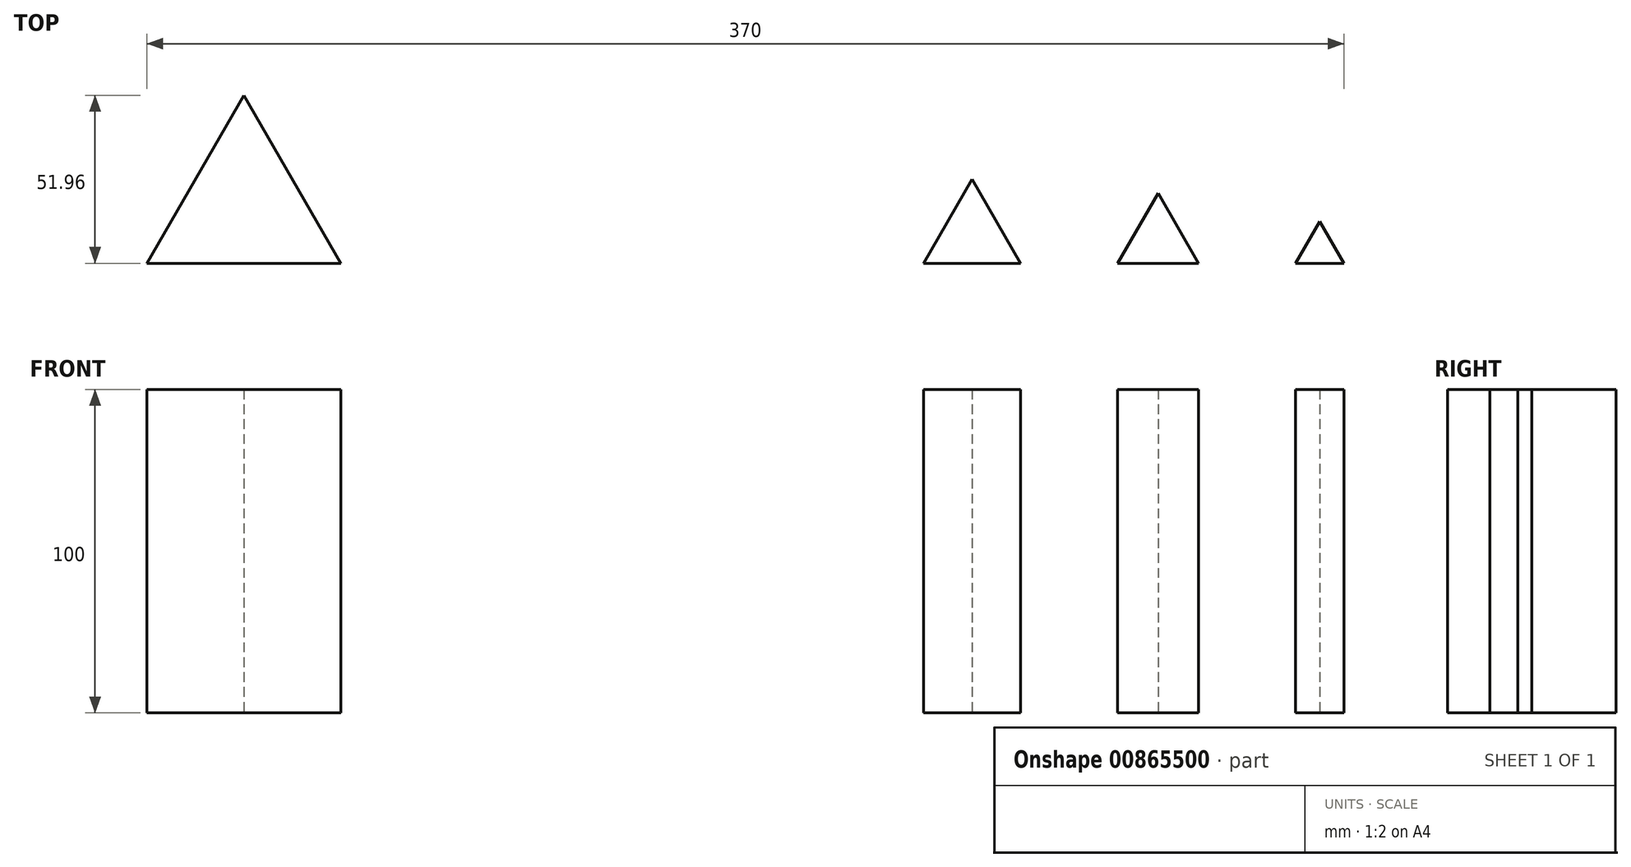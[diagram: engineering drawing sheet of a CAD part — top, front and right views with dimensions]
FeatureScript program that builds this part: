
annotation { "Feature Type Name" : "Feature", "Feature Type Description" : "" }
export const myFeature = defineFeature(function(context is Context, id is Id, definition is map)
    precondition{}
    {
        {
            var Q0;
            Q0=qCreatedBy(makeId("Top.planeOp"),FACE);
            var sketch = newSketch(context, id + "F0", { "sketchPlane" : qUnion([Q0])});
            skLineSegment(sketch, "E0.bottom", {"start": v(0, 0) * mm, "end": v(450, 0) * mm});
            skLineSegment(sketch, "E0.top", {"start": v(0, -450) * mm, "end": v(450, -450) * mm});
            skLineSegment(sketch, "E0.left", {"start": v(0, 0) * mm, "end": v(0, -450) * mm});
            skLineSegment(sketch, "E0.right", {"start": v(450, 0) * mm, "end": v(450, -450) * mm});
            skCircle(sketch, "E1", {"center": v(32.5, 0) * mm, "radius": 7.5 * mm});
            skCircle(sketch, "E2", {"center": v(70, 0) * mm, "radius": 10 * mm});
            skCircle(sketch, "E3", {"center": v(112.5, 0) * mm, "radius": 12.5 * mm});
            skCircle(sketch, "E4", {"center": v(212.5, 0) * mm, "radius": 17.5 * mm});
            skCircle(sketch, "E5", {"center": v(270, 0) * mm, "radius": 20 * mm});
            skPoint(sketch, "E6", {"position": v(0, -225) * mm});
            skCircle(sketch, "E7", {"center": v(160, 0) * mm, "radius": 15 * mm});
            skCircle(sketch, "E8", {"center": v(332.5, 0) * mm, "radius": 22.5 * mm});
            skCircle(sketch, "E9", {"center": v(400, 0) * mm, "radius": 25 * mm});
            skCircle(sketch, "E10", {"center": v(0, -50) * mm, "radius": 27.5 * mm});
            skCircle(sketch, "E11", {"center": v(0, -127.5) * mm, "radius": 30 * mm});
            skCircle(sketch, "E12", {"center": v(0, -210) * mm, "radius": 32.5 * mm});
            skCircle(sketch, "E13", {"center": v(0, -297.5) * mm, "radius": 35 * mm});
            skCircle(sketch, "E14", {"center": v(0, -390) * mm, "radius": 37.5 * mm});
            skCircle(sketch, "E15.cCircle", {"center": v(450, -45) * mm, "radius": 20 * mm, "construction": true});
            skLineSegment(sketch, "E15.0", {"start": v(450, -65) * mm, "end": v(432.68, -55) * mm});
            skLineSegment(sketch, "E15.1", {"start": v(432.68, -55) * mm, "end": v(432.68, -35) * mm});
            skLineSegment(sketch, "E15.2", {"start": v(432.68, -35) * mm, "end": v(450, -25) * mm});
            skLineSegment(sketch, "E15.3", {"start": v(450, -25) * mm, "end": v(467.32, -35) * mm});
            skLineSegment(sketch, "E15.4", {"start": v(467.32, -35) * mm, "end": v(467.32, -55) * mm});
            skLineSegment(sketch, "E15.5", {"start": v(467.32, -55) * mm, "end": v(450, -65) * mm});
            skCircle(sketch, "E16.cCircle", {"center": v(450, -120) * mm, "radius": 34.64 * mm, "construction": true});
            skLineSegment(sketch, "E16.0", {"start": v(420.17, -137.61) * mm, "end": v(419.83, -102.97) * mm});
            skLineSegment(sketch, "E16.1", {"start": v(419.83, -102.97) * mm, "end": v(449.66, -85.36) * mm});
            skLineSegment(sketch, "E16.2", {"start": v(449.66, -85.36) * mm, "end": v(479.83, -102.39) * mm});
            skLineSegment(sketch, "E16.3", {"start": v(479.83, -102.39) * mm, "end": v(480.17, -137.03) * mm});
            skLineSegment(sketch, "E16.4", {"start": v(480.17, -137.03) * mm, "end": v(450.34, -154.64) * mm});
            skLineSegment(sketch, "E16.5", {"start": v(450.34, -154.64) * mm, "end": v(420.17, -137.61) * mm});
            skCircle(sketch, "E17.cCircle", {"center": v(450, -225) * mm, "radius": 46.19 * mm, "construction": true});
            skLineSegment(sketch, "E17.0", {"start": v(410.35, -248.7) * mm, "end": v(409.66, -202.51) * mm});
            skLineSegment(sketch, "E17.1", {"start": v(409.66, -202.51) * mm, "end": v(449.3, -178.82) * mm});
            skLineSegment(sketch, "E17.2", {"start": v(449.3, -178.82) * mm, "end": v(489.65, -201.3) * mm});
            skLineSegment(sketch, "E17.3", {"start": v(489.65, -201.3) * mm, "end": v(490.34, -247.49) * mm});
            skLineSegment(sketch, "E17.4", {"start": v(490.34, -247.49) * mm, "end": v(450.7, -271.18) * mm});
            skLineSegment(sketch, "E17.5", {"start": v(450.7, -271.18) * mm, "end": v(410.35, -248.7) * mm});
            skCircle(sketch, "E18.cCircle", {"center": v(450, -360) * mm, "radius": 57.74 * mm, "construction": true});
            skLineSegment(sketch, "E18.0", {"start": v(400.24, -330.72) * mm, "end": v(450.48, -302.27) * mm});
            skLineSegment(sketch, "E18.1", {"start": v(450.48, -302.27) * mm, "end": v(500.24, -331.55) * mm});
            skLineSegment(sketch, "E18.2", {"start": v(500.24, -331.55) * mm, "end": v(499.76, -389.28) * mm});
            skLineSegment(sketch, "E18.3", {"start": v(499.76, -389.28) * mm, "end": v(449.52, -417.73) * mm});
            skLineSegment(sketch, "E18.4", {"start": v(449.52, -417.73) * mm, "end": v(399.76, -388.45) * mm});
            skLineSegment(sketch, "E18.5", {"start": v(399.76, -388.45) * mm, "end": v(400.24, -330.72) * mm});
            skLineSegment(sketch, "E19", {"start": v(420, -450) * mm, "end": v(412.5, -437) * mm});
            skLineSegment(sketch, "E20", {"start": v(412.5, -437) * mm, "end": v(405, -450) * mm});
            skLineSegment(sketch, "E21", {"start": v(420, -450) * mm, "end": v(405, -450) * mm});
            skLineSegment(sketch, "E22", {"start": v(375, -450) * mm, "end": v(362.5, -428.35) * mm});
            skLineSegment(sketch, "E23", {"start": v(362.5, -428.35) * mm, "end": v(350, -450) * mm});
            skLineSegment(sketch, "E24", {"start": v(350, -450) * mm, "end": v(375, -450) * mm});
            skLineSegment(sketch, "E25", {"start": v(320, -450) * mm, "end": v(305, -424.02) * mm});
            skLineSegment(sketch, "E26", {"start": v(305, -424.02) * mm, "end": v(290, -450) * mm});
            skLineSegment(sketch, "E27", {"start": v(290, -450) * mm, "end": v(320, -450) * mm});
            skLineSegment(sketch, "E28", {"start": v(260, -450) * mm, "end": v(220, -450) * mm});
            skLineSegment(sketch, "E29", {"start": v(220, -450) * mm, "end": v(240, -415.36) * mm});
            skLineSegment(sketch, "E30", {"start": v(240, -415.36) * mm, "end": v(260, -450) * mm});
            skLineSegment(sketch, "E31", {"start": v(190, -450) * mm, "end": v(140, -450) * mm});
            skLineSegment(sketch, "E32", {"start": v(140, -450) * mm, "end": v(165, -406.7) * mm});
            skLineSegment(sketch, "E33", {"start": v(165, -406.7) * mm, "end": v(190, -450) * mm});
            skLineSegment(sketch, "E34", {"start": v(110, -450) * mm, "end": v(50, -450) * mm});
            skLineSegment(sketch, "E35", {"start": v(50, -450) * mm, "end": v(80, -398.04) * mm});
            skLineSegment(sketch, "E36", {"start": v(80, -398.04) * mm, "end": v(110, -450) * mm});
            skCircle(sketch, "E37", {"center": v(366.86, -63.19) * mm, "radius": 8.5 * mm});
            skCircle(sketch, "E38", {"center": v(306.86, -63.19) * mm, "radius": 11.5 * mm});
            skCircle(sketch, "E39", {"center": v(237.86, -63.19) * mm, "radius": 17.5 * mm});
            skCircle(sketch, "E40", {"center": v(172.86, -63.19) * mm, "radius": 22.5 * mm});
            skCircle(sketch, "E41", {"center": v(90.36, -63.19) * mm, "radius": 30 * mm});
            skPoint(sketch, "E42.cornerSnap0", {"position": v(400, -359.59) * mm});
            skEllipse(sketch, "E43", {"center": v(355, -158.3) * mm, "majorRadius": 69.57 * mm, "minorRadius": 24.91 * mm, "majorAxis": v(0, -1)});
            skEllipse(sketch, "E44", {"center": v(255, -158.3) * mm, "majorRadius": 57.98 * mm, "minorRadius": 25.3 * mm, "majorAxis": v(0, -1)});
            skEllipse(sketch, "E45", {"center": v(160, -158.3) * mm, "majorRadius": 47.06 * mm, "minorRadius": 19.98 * mm, "majorAxis": v(0, -1)});
            skEllipse(sketch, "E46", {"center": v(75, -158.3) * mm, "majorRadius": 42.97 * mm, "minorRadius": 16.37 * mm, "majorAxis": v(0, -1)});
            skLineSegment(sketch, "E47.bottom", {"start": v(132.9, -316.06) * mm, "end": v(52.9, -316.06) * mm});
            skLineSegment(sketch, "E47.top", {"start": v(132.9, -236.06) * mm, "end": v(52.9, -236.06) * mm});
            skLineSegment(sketch, "E47.left", {"start": v(132.9, -316.06) * mm, "end": v(132.9, -236.06) * mm});
            skLineSegment(sketch, "E47.right", {"start": v(52.9, -316.06) * mm, "end": v(52.9, -236.06) * mm});
            skPoint(sketch, "E47.middle", {"position": v(92.9, -276.06) * mm});
            skLineSegment(sketch, "E48.bottom", {"start": v(232.94, -306.06) * mm, "end": v(172.94, -306.06) * mm});
            skLineSegment(sketch, "E48.top", {"start": v(232.94, -246.06) * mm, "end": v(172.94, -246.06) * mm});
            skLineSegment(sketch, "E48.left", {"start": v(232.94, -306.06) * mm, "end": v(232.94, -246.06) * mm});
            skLineSegment(sketch, "E48.right", {"start": v(172.94, -306.06) * mm, "end": v(172.94, -246.06) * mm});
            skPoint(sketch, "E48.middle", {"position": v(202.94, -276.06) * mm});
            skLineSegment(sketch, "E49.bottom", {"start": v(312.28, -296.06) * mm, "end": v(272.28, -296.06) * mm});
            skLineSegment(sketch, "E49.top", {"start": v(312.28, -256.06) * mm, "end": v(272.28, -256.06) * mm});
            skLineSegment(sketch, "E49.left", {"start": v(312.28, -296.06) * mm, "end": v(312.28, -256.06) * mm});
            skLineSegment(sketch, "E49.right", {"start": v(272.28, -296.06) * mm, "end": v(272.28, -256.06) * mm});
            skPoint(sketch, "E49.middle", {"position": v(292.28, -276.06) * mm});
            skLineSegment(sketch, "E50.bottom", {"start": v(372.3, -286.06) * mm, "end": v(352.3, -286.06) * mm});
            skLineSegment(sketch, "E50.top", {"start": v(372.3, -266.06) * mm, "end": v(352.3, -266.06) * mm});
            skLineSegment(sketch, "E50.left", {"start": v(372.3, -286.06) * mm, "end": v(372.3, -266.06) * mm});
            skLineSegment(sketch, "E50.right", {"start": v(352.3, -286.06) * mm, "end": v(352.3, -266.06) * mm});
            skPoint(sketch, "E50.middle", {"position": v(362.3, -276.06) * mm});
            skLineSegment(sketch, "E51.bottom", {"start": v(80, -382.47) * mm, "end": v(60, -382.47) * mm});
            skLineSegment(sketch, "E51.top", {"start": v(80, -372.47) * mm, "end": v(60, -372.47) * mm});
            skLineSegment(sketch, "E51.left", {"start": v(80, -382.47) * mm, "end": v(80, -372.47) * mm});
            skLineSegment(sketch, "E51.right", {"start": v(60, -382.47) * mm, "end": v(60, -372.47) * mm});
            skPoint(sketch, "E51.middle", {"position": v(70, -377.47) * mm});
            skLineSegment(sketch, "E52.bottom", {"start": v(110, -387.47) * mm, "end": v(150, -387.47) * mm});
            skLineSegment(sketch, "E52.top", {"start": v(110, -367.47) * mm, "end": v(150, -367.47) * mm});
            skLineSegment(sketch, "E52.left", {"start": v(110, -387.47) * mm, "end": v(110, -367.47) * mm});
            skLineSegment(sketch, "E52.right", {"start": v(150, -387.47) * mm, "end": v(150, -367.47) * mm});
            skPoint(sketch, "E52.middle", {"position": v(130, -377.47) * mm});
            skLineSegment(sketch, "E53.bottom", {"start": v(190, -392.47) * mm, "end": v(250, -392.47) * mm});
            skLineSegment(sketch, "E53.top", {"start": v(190, -362.47) * mm, "end": v(250, -362.47) * mm});
            skLineSegment(sketch, "E53.left", {"start": v(190, -392.47) * mm, "end": v(190, -362.47) * mm});
            skLineSegment(sketch, "E53.right", {"start": v(250, -392.47) * mm, "end": v(250, -362.47) * mm});
            skPoint(sketch, "E53.middle", {"position": v(220, -377.47) * mm});
            skLineSegment(sketch, "E54.bottom", {"start": v(375, -397.47) * mm, "end": v(295, -397.47) * mm});
            skLineSegment(sketch, "E54.top", {"start": v(375, -357.47) * mm, "end": v(295, -357.47) * mm});
            skLineSegment(sketch, "E54.left", {"start": v(375, -397.47) * mm, "end": v(375, -357.47) * mm});
            skLineSegment(sketch, "E54.right", {"start": v(295, -397.47) * mm, "end": v(295, -357.47) * mm});
            skPoint(sketch, "E54.middle", {"position": v(335, -377.47) * mm});
            skLineSegment(sketch, "E55", {"start": v(0, 0) * mm, "end": v(-63.64, 63.64) * mm});
            skLineSegment(sketch, "E56", {"start": v(-63.64, 63.64) * mm, "end": v(513.64, 63.64) * mm});
            skLineSegment(sketch, "E57", {"start": v(513.64, 63.64) * mm, "end": v(450, 0) * mm});
            skLineSegment(sketch, "E58", {"start": v(513.64, 63.64) * mm, "end": v(513.64, -513.64) * mm});
            skLineSegment(sketch, "E59", {"start": v(513.64, -513.64) * mm, "end": v(450, -450) * mm});
            skLineSegment(sketch, "E60", {"start": v(-63.64, 63.64) * mm, "end": v(-63.64, -513.64) * mm});
            skLineSegment(sketch, "E61", {"start": v(-63.64, -513.64) * mm, "end": v(0, -450) * mm});
            skLineSegment(sketch, "E62", {"start": v(-63.64, -513.64) * mm, "end": v(513.64, -513.64) * mm});
            skSolve(sketch);
        }
        {
            var Q0;
            {var subQ0=sQuery(id+"F0.wireOp",EDGE,"E21");Q0=makeQuery(id+"F0.imprint","IMPRINT",FACE,{"disambiguationData":[TD([[makeQuery(id+"F0.imprint","IMPRINT",EDGE,{"derivedFrom":subQ0}),1.0]])]});}
            var Q1;
            Q1=makeQuery(id+"F0.imprint","IMPRINT",FACE,{"disambiguationData":[TD([[makeQuery(id+"F0.imprint","IMPRINT",EDGE,{"derivedFrom":sQuery(id+"F0.wireOp",EDGE,"E35")}),-1.0]])]});
            var Q2;
            Q2=makeQuery(id+"F0.imprint","IMPRINT",FACE,{"disambiguationData":[TD([[makeQuery(id+"F0.imprint","IMPRINT",EDGE,{"derivedFrom":sQuery(id+"F0.wireOp",EDGE,"E31")}),-1.0]])]});
            var Q3;
            Q3=makeQuery(id+"F0.imprint","IMPRINT",FACE,{"disambiguationData":[TD([[makeQuery(id+"F0.imprint","IMPRINT",EDGE,{"derivedFrom":sQuery(id+"F0.wireOp",EDGE,"E28")}),-1.0]])]});
            var Q4;
            Q4=makeQuery(id+"F0.imprint","IMPRINT",FACE,{"disambiguationData":[TD([[makeQuery(id+"F0.imprint","IMPRINT",EDGE,{"derivedFrom":sQuery(id+"F0.wireOp",EDGE,"E25")}),1.0]])]});
            var Q5;
            Q5=makeQuery(id+"F0.imprint","IMPRINT",FACE,{"disambiguationData":[TD([[makeQuery(id+"F0.imprint","IMPRINT",EDGE,{"derivedFrom":sQuery(id+"F0.wireOp",EDGE,"E22")}),1.0]])]});
            var Q6;
            Q6=makeQuery(id+"F0.imprint","IMPRINT",FACE,{"disambiguationData":[TD([[makeQuery(id+"F0.imprint","IMPRINT",EDGE,{"derivedFrom":sQuery(id+"F0.wireOp",EDGE,"E19")}),1.0]])]});
            extrude(context, id + "F1", {"entities" : qUnion([Q0, Q1, Q2, Q3, Q4, Q5, Q6]), "depth" : 100 * mm, "offsetDistance" : 25 * mm});
        }
    });
